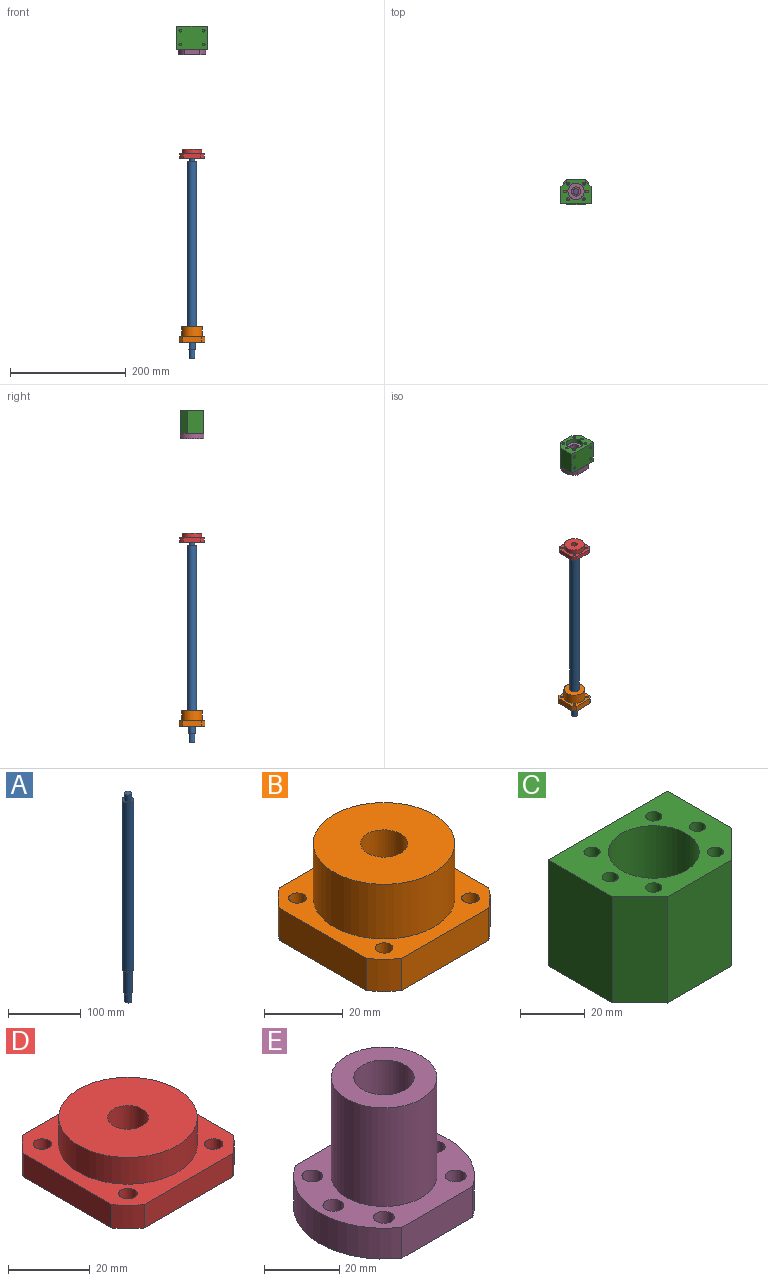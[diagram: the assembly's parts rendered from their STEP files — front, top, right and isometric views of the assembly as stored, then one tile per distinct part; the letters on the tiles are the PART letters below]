
ASSEMBLY  parts=5 mates=6
PART A: 9 faces, bbox 16x16x350 mm
  f0: cylinder r=5mm len=11mm, axis (0,0,-1), area 345.6mm2, adj f1,f2
  f1: plane 10x10mm, normal (0,0,1), area 78.5mm2, adj f0
  f2: plane 16x16mm, normal (0,0,1), area 122.5mm2, adj f0,f4
  f3: plane 16x16mm, normal (0,0,-1), area 88mm2, adj f4,f5
  f4: cylinder r=8mm len=285mm, axis (0,0,-1), area 14325.7mm2, adj f2,f3
  f5: cylinder r=6mm len=39mm, axis (0,0,-1), area 1470.3mm2, adj f3,f6
  f6: plane 12x12mm, normal (0,0,-1), area 34.6mm2, adj f5,f8
  f7: plane 10x10mm, normal (0,0,-1), area 78.5mm2, adj f8
  f8: cylinder r=5mm len=15mm, axis (0,0,-1), area 471.2mm2, adj f6,f7
PART B: 25 faces, bbox 44x44x27 mm
  f0: cylinder r=4mm len=8mm, axis (0,0,-1), area 100.5mm2, adj f14,f22
  f1: cylinder r=4mm len=8mm, axis (0,0,-1), area 100.5mm2, adj f14,f20
  f2: cylinder r=4mm len=8mm, axis (0,0,-1), area 100.5mm2, adj f14,f18
  f3: cylinder r=4mm len=8mm, axis (0,0,-1), area 100.5mm2, adj f14,f16
  f4: plane 31.31x10mm, normal (1,0,0), area 313mm2, adj f5,f11,f13,f14
  f5: cylinder r=27mm len=10mm, axis (0,0,-1), area 90.2mm2, adj f4,f6,f13,f14
  f6: plane 31.31x10mm, normal (0,1,0), area 313mm2, adj f5,f7,f13,f14
  f7: cylinder r=27mm len=10mm, axis (0,0,-1), area 90.2mm2, adj f6,f8,f13,f14
  f8: plane 31.31x10mm, normal (-1,0,0), area 313mm2, adj f7,f9,f13,f14
  f9: cylinder r=27mm len=10mm, axis (0,0,-1), area 90.2mm2, adj f8,f10,f13,f14
  f10: plane 31.31x10mm, normal (0,-1,0), area 313mm2, adj f9,f11,f13,f14
  f11: cylinder r=27mm len=10mm, axis (0,0,-1), area 90.2mm2, adj f4,f10,f13,f14
  f12: cylinder r=6mm len=27mm, axis (0,0,-1), area 1017.9mm2, adj f14,f24
  f13: plane 44x44mm, normal (0,0,1), area 782.9mm2, adj f4,f5,f6,f7,f8,f9,f10,f11
  f14: plane 44x44mm, normal (0,0,-1), area 1550.3mm2, adj f0,f1,f2,f3,f4,f5,f6,f7
  f15: cylinder r=2.25mm len=6mm, axis (0,0,-1), area 84.8mm2, adj f13,f16
  f16: plane 8x8mm, normal (0,0,-1), area 34.4mm2, adj f3,f15
  f17: cylinder r=2.25mm len=6mm, axis (0,0,-1), area 84.8mm2, adj f13,f18
  f18: plane 8x8mm, normal (0,0,-1), area 34.4mm2, adj f2,f17
  f19: cylinder r=2.25mm len=6mm, axis (0,0,-1), area 84.8mm2, adj f13,f20
  f20: plane 8x8mm, normal (0,0,-1), area 34.4mm2, adj f1,f19
  f21: cylinder r=2.25mm len=6mm, axis (0,0,-1), area 84.8mm2, adj f13,f22
  f22: plane 8x8mm, normal (0,0,-1), area 34.4mm2, adj f0,f21
  f23: cylinder r=18mm len=36mm, axis (0,0,-1), area 1922.7mm2, adj f13,f24
  f24: plane 36x36mm, normal (0,0,1), area 904.8mm2, adj f12,f23
PART C: 23 faces, bbox 52x40x40 mm
  f0: plane 52x40mm, normal (0,1,0), area 2001.5mm2, adj f1,f11,f13,f14,f15,f17,f19,f21
  f1: plane 40x28mm, normal (-1,0,0), area 1120mm2, adj f0,f2,f13,f14
  f2: plane 40x12mm, normal (-0.71,-0.71,0), area 678.8mm2, adj f1,f3,f13,f14
  f3: plane 40x28mm, normal (0,-1,0), area 1120mm2, adj f2,f4,f13,f14
  f4: plane 40x12mm, normal (0.71,-0.71,0), area 678.8mm2, adj f3,f11,f13,f14
  f5: cylinder r=2.5mm len=40mm, axis (0,0,-1), area 628.3mm2, adj f13,f14
  f6: cylinder r=2.5mm len=40mm, axis (0,0,-1), area 628.3mm2, adj f13,f14
  f7: cylinder r=2.5mm len=40mm, axis (0,0,-1), area 628.3mm2, adj f13,f14
  f8: cylinder r=2.5mm len=40mm, axis (0,0,-1), area 628.3mm2, adj f13,f14
  f9: cylinder r=2.5mm len=40mm, axis (0,0,-1), area 628.3mm2, adj f13,f14
  f10: cylinder r=14mm len=40mm, axis (0,0,-1), area 3518.6mm2, adj f13,f14
  f11: plane 40x28mm, normal (1,0,0), area 1120mm2, adj f0,f4,f13,f14
  f12: cylinder r=2.5mm len=40mm, axis (0,0,-1), area 628.3mm2, adj f13,f14
  f13: plane 52x40mm, normal (0,0,1), area 1202.4mm2, adj f0,f1,f2,f3,f4,f5,f6,f7
  f14: plane 52x40mm, normal (0,0,-1), area 1202.4mm2, adj f0,f1,f2,f3,f4,f5,f6,f7
  f15: cylinder r=2.5mm len=15mm, axis (0,1,0), area 235.6mm2, adj f0,f16
  f16: plane 5x5mm, normal (0,1,0), area 19.6mm2, adj f15
  f17: cylinder r=2.5mm len=15mm, axis (0,1,0), area 235.6mm2, adj f0,f18
  f18: plane 5x5mm, normal (0,1,0), area 19.6mm2, adj f17
  f19: cylinder r=2.5mm len=15mm, axis (0,1,0), area 235.6mm2, adj f0,f20
  f20: plane 5x5mm, normal (0,1,0), area 19.6mm2, adj f19
  f21: cylinder r=2.5mm len=15mm, axis (0,1,0), area 235.6mm2, adj f0,f22
  f22: plane 5x5mm, normal (0,1,0), area 19.6mm2, adj f21
PART D: 25 faces, bbox 42x42x15 mm
  f0: cylinder r=4mm len=8mm, axis (0,0,-1), area 100.5mm2, adj f14,f22
  f1: cylinder r=4mm len=8mm, axis (0,0,-1), area 100.5mm2, adj f14,f20
  f2: cylinder r=4mm len=8mm, axis (0,0,-1), area 100.5mm2, adj f14,f18
  f3: cylinder r=4mm len=8mm, axis (0,0,-1), area 100.5mm2, adj f14,f16
  f4: plane 30.66x7mm, normal (1,0,0), area 214.6mm2, adj f5,f11,f13,f14
  f5: cylinder r=26mm len=7mm, axis (0,0,-1), area 56.4mm2, adj f4,f6,f13,f14
  f6: plane 30.66x7mm, normal (0,1,0), area 214.6mm2, adj f5,f7,f13,f14
  f7: cylinder r=26mm len=7mm, axis (0,0,-1), area 56.4mm2, adj f6,f8,f13,f14
  f8: plane 30.66x7mm, normal (-1,0,0), area 214.6mm2, adj f7,f9,f13,f14
  f9: cylinder r=26mm len=7mm, axis (0,0,-1), area 56.4mm2, adj f8,f10,f13,f14
  f10: plane 30.66x7mm, normal (0,-1,0), area 214.6mm2, adj f9,f11,f13,f14
  f11: cylinder r=26mm len=7mm, axis (0,0,-1), area 56.4mm2, adj f4,f10,f13,f14
  f12: cylinder r=5mm len=15mm, axis (0,0,-1), area 471.2mm2, adj f14,f24
  f13: plane 42x42mm, normal (0,0,1), area 734.8mm2, adj f4,f5,f6,f7,f8,f9,f10,f11
  f14: plane 42x42mm, normal (0,0,-1), area 1426.8mm2, adj f0,f1,f2,f3,f4,f5,f6,f7
  f15: cylinder r=2.25mm len=4.5mm, axis (0,0,-1), area 42.4mm2, adj f13,f16
  f16: plane 8x8mm, normal (0,0,-1), area 34.4mm2, adj f3,f15
  f17: cylinder r=2.25mm len=4.5mm, axis (0,0,-1), area 42.4mm2, adj f13,f18
  f18: plane 8x8mm, normal (0,0,-1), area 34.4mm2, adj f2,f17
  f19: cylinder r=2.25mm len=4.5mm, axis (0,0,-1), area 42.4mm2, adj f13,f20
  f20: plane 8x8mm, normal (0,0,-1), area 34.4mm2, adj f1,f19
  f21: cylinder r=2.25mm len=4.5mm, axis (0,0,-1), area 42.4mm2, adj f13,f22
  f22: plane 8x8mm, normal (0,0,-1), area 34.4mm2, adj f0,f21
  f23: cylinder r=17mm len=34mm, axis (0,0,-1), area 854.5mm2, adj f13,f24
  f24: plane 34x34mm, normal (0,0,1), area 829.4mm2, adj f12,f23
PART E: 15 faces, bbox 48x40x42 mm
  f0: plane 26.53x10mm, normal (0,1,0), area 265.3mm2, adj f1,f3,f11,f12
  f1: cylinder r=24mm len=40mm, axis (0,0,-1), area 472.9mm2, adj f0,f2,f11,f12
  f2: plane 26.53x10mm, normal (0,-1,0), area 265.3mm2, adj f1,f3,f11,f12
  f3: cylinder r=24mm len=40mm, axis (0,0,-1), area 472.9mm2, adj f0,f2,f11,f12
  f4: cylinder r=2.75mm len=10mm, axis (0,0,-1), area 172.8mm2, adj f11,f12
  f5: cylinder r=2.75mm len=10mm, axis (0,0,-1), area 172.8mm2, adj f11,f12
  f6: cylinder r=2.75mm len=10mm, axis (0,0,-1), area 172.8mm2, adj f11,f12
  f7: cylinder r=2.75mm len=10mm, axis (0,0,-1), area 172.8mm2, adj f11,f12
  f8: cylinder r=2.75mm len=10mm, axis (0,0,-1), area 172.8mm2, adj f11,f12
  f9: cylinder r=2.75mm len=10mm, axis (0,0,-1), area 172.8mm2, adj f11,f12
  f10: cylinder r=8mm len=42mm, axis (0,0,-1), area 2111.2mm2, adj f12,f14
  f11: plane 48x40mm, normal (0,0,1), area 907.2mm2, adj f0,f1,f2,f3,f4,f5,f6,f7
  f12: plane 48x40mm, normal (0,0,-1), area 1321.9mm2, adj f0,f1,f2,f3,f4,f5,f6,f7
  f13: cylinder r=14mm len=32mm, axis (0,0,-1), area 2814.9mm2, adj f11,f14
  f14: plane 28x28mm, normal (0,0,1), area 414.7mm2, adj f10,f13
PLACE A t=(-2.27,-0.45,960.2)mm
PLACE B t=(-15.4,-246.76,987.2)mm
PLACE C rot(axis=(1,0,0),180deg) t=(-120.9,55.75,1533)mm
PLACE D t=(-105.01,-247.6,1305.2)mm
PLACE E t=(-19.88,74.23,1483)mm
MATE parallel D.f10 <-> B.f10  axis (0,-1,0) through (-51.13,13.99,1308.7)mm
MATE cylindrical D.f5 <-> A.f0  axis (0,0,-1) through (-51.13,34.99,1312.7)mm
MATE parallel D.f5 <-> A.f0  axis (0,0,-1) through (-51.13,34.99,1305.2)mm
MATE planar B.f5 <-> A.f0  axis (0,0,1) through (-51.13,34.99,1014.2)mm
MATE cylindrical E.f1 <-> A.f0  axis (0,0,-1) through (-51.13,34.99,1504)mm
MATE cylindrical B.f5 <-> A.f0  axis (0,0,-1) through (-51.13,34.99,1014.2)mm
